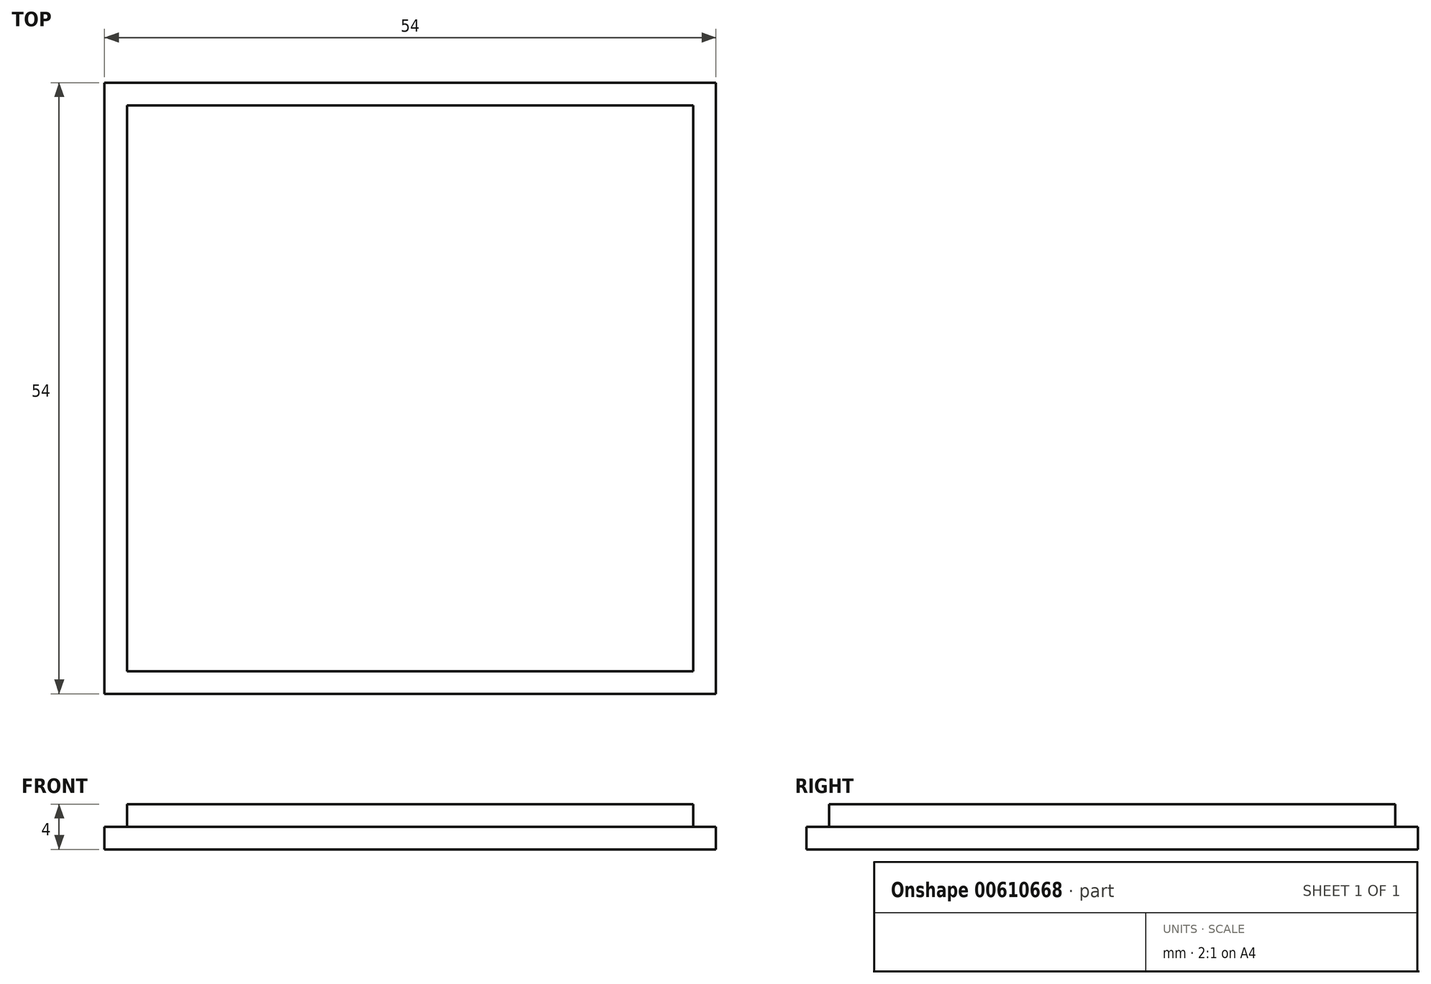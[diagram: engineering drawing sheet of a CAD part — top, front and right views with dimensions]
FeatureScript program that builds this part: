
annotation { "Feature Type Name" : "Feature", "Feature Type Description" : "" }
export const myFeature = defineFeature(function(context is Context, id is Id, definition is map)
    precondition{}
    {
        {
            var Q0;
            Q0=qCreatedBy(makeId("Top.planeOp"),FACE);
            var sketch = newSketch(context, id + "F0", { "sketchPlane" : qUnion([Q0])});
            skLineSegment(sketch, "E0.bottom", {"start": v(25, 25) * mm, "end": v(-25, 25) * mm});
            skLineSegment(sketch, "E0.top", {"start": v(25, -25) * mm, "end": v(-25, -25) * mm});
            skLineSegment(sketch, "E0.left", {"start": v(25, 25) * mm, "end": v(25, -25) * mm});
            skLineSegment(sketch, "E0.right", {"start": v(-25, 25) * mm, "end": v(-25, -25) * mm});
            skPoint(sketch, "E0.middle", {"position": v(0, 0) * mm});
            skLineSegment(sketch, "E1.0", {"start": v(27, 27) * mm, "end": v(-27, 27) * mm});
            skLineSegment(sketch, "E1.1", {"start": v(27, 27) * mm, "end": v(27, -27) * mm});
            skLineSegment(sketch, "E1.2", {"start": v(27, -27) * mm, "end": v(-27, -27) * mm});
            skLineSegment(sketch, "E1.3", {"start": v(-27, 27) * mm, "end": v(-27, -27) * mm});
            skSolve(sketch);
        }
        {
            var Q0;
            Q0=makeQuery(id+"F0.imprint","IMPRINT",FACE,{"disambiguationData":[TD([[makeQuery(id+"F0.imprint","IMPRINT",EDGE,{"derivedFrom":sQuery(id+"F0.wireOp",EDGE,"E0.bottom")}),1.0]])]});
            extrude(context, id + "F1", {"entities" : qUnion([Q0]), "depth" : 4 * mm, "offsetDistance" : 25 * mm});
        }
        {
            var Q0;
            Q0=makeQuery(id+"F0.imprint","IMPRINT",FACE,{"disambiguationData":[TD([[makeQuery(id+"F0.imprint","IMPRINT",EDGE,{"derivedFrom":sQuery(id+"F0.wireOp",EDGE,"E0.bottom")}),-1.0]])]});
            extrude(context, id + "F2", {"entities" : qUnion([Q0]), "operationType" : NewBodyOperationType.ADD, "depth" : 2 * mm, "offsetDistance" : 25 * mm});
        }
    });
